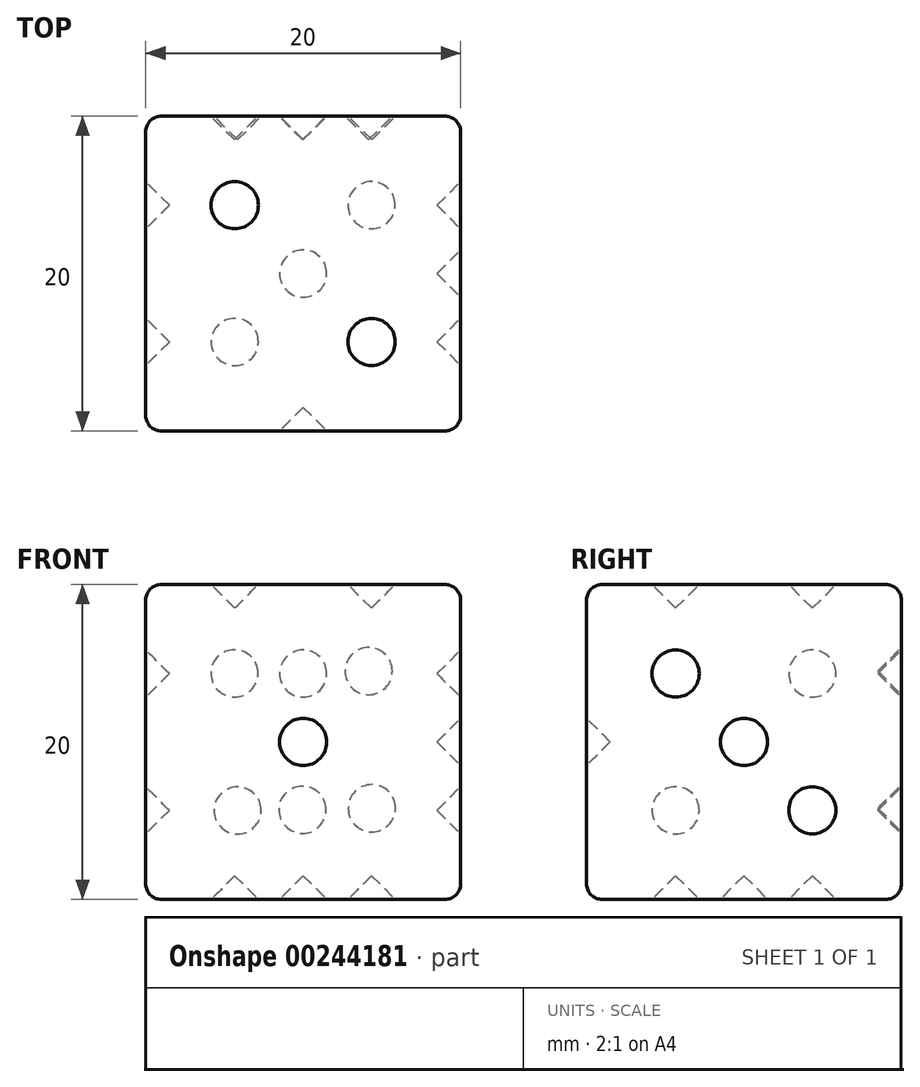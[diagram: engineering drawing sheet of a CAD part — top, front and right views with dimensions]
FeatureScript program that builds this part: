
annotation { "Feature Type Name" : "Feature", "Feature Type Description" : "" }
export const myFeature = defineFeature(function(context is Context, id is Id, definition is map)
    precondition{}
    {
        {
            var Q0;
            Q0=qCreatedBy(makeId("Top.planeOp"),FACE);
            var sketch = newSketch(context, id + "F0", { "sketchPlane" : qUnion([Q0])});
            skLineSegment(sketch, "E0.bottom", {"start": v(0, 0) * mm, "end": v(20, 0) * mm});
            skLineSegment(sketch, "E0.top", {"start": v(0, 20) * mm, "end": v(20, 20) * mm});
            skLineSegment(sketch, "E0.left", {"start": v(0, 0) * mm, "end": v(0, 20) * mm});
            skLineSegment(sketch, "E0.right", {"start": v(20, 0) * mm, "end": v(20, 20) * mm});
            skSolve(sketch);
        }
        {
            var Q0;
            Q0 = qSketchRegion(id + "F0", true);
            extrude(context, id + "F1", {"entities" : qUnion([Q0]), "depth" : 20 * mm});
        }
        {
            var Q0;
            Q0=makeQuery(id+"F1.opExtrude","SWEPT_FACE",FACE,{"disambiguationData":[OSD([sQuery(id+"F0.wireOp",EDGE,"E0.bottom")])]});
            var sketch = newSketch(context, id + "F2", { "sketchPlane" : qUnion([Q0])});
            skLineSegment(sketch, "E1", {"start": v(10, 20) * mm, "end": v(10, 0) * mm, "construction": true});
            skCircle(sketch, "E2", {"center": v(10, 10) * mm, "radius": 1.5 * mm});
            skSolve(sketch);
        }
        {
            var Q0;
            Q0 = qSketchRegion(id + "F2", true);
            extrude(context, id + "F3", {"entities" : qUnion([Q0]), "operationType" : NewBodyOperationType.REMOVE, "oppositeDirection" : true, "depth" : 1.5 * mm});
        }
        {
            var Q0;
            Q0=makeQuery(id+"F1.opExtrude","CAP_EDGE",EDGE,{"disambiguationData":[OSD([sQuery(id+"F0.wireOp",EDGE,"E0.bottom")])],"isStart":false});
            var Q1;
            Q1=makeQuery(id+"F1.opExtrude","CAP_EDGE",EDGE,{"disambiguationData":[OSD([sQuery(id+"F0.wireOp",EDGE,"E0.right")])],"isStart":false});
            var Q2;
            Q2=makeQuery(id+"F1.opExtrude","SWEPT_EDGE",EDGE,{"disambiguationData":[OSD([sQuery(id+"F0.wireOp",EDGE,"E0.bottom"),sQuery(id+"F0.wireOp",EDGE,"E0.right")])]});
            var Q3;
            Q3=makeQuery(id+"F1.opExtrude","SWEPT_EDGE",EDGE,{"disambiguationData":[OSD([sQuery(id+"F0.wireOp",EDGE,"E0.bottom"),sQuery(id+"F0.wireOp",EDGE,"E0.left")])]});
            var Q4;
            Q4=makeQuery(id+"F1.opExtrude","CAP_EDGE",EDGE,{"disambiguationData":[OSD([sQuery(id+"F0.wireOp",EDGE,"E0.bottom")])],"isStart":true});
            var Q5;
            Q5=makeQuery(id+"F1.opExtrude","CAP_EDGE",EDGE,{"disambiguationData":[OSD([sQuery(id+"F0.wireOp",EDGE,"E0.right")])],"isStart":true});
            var Q6;
            Q6=makeQuery(id+"F1.opExtrude","CAP_EDGE",EDGE,{"disambiguationData":[OSD([sQuery(id+"F0.wireOp",EDGE,"E0.left")])],"isStart":false});
            var Q7;
            Q7=makeQuery(id+"F1.opExtrude","CAP_EDGE",EDGE,{"disambiguationData":[OSD([sQuery(id+"F0.wireOp",EDGE,"E0.top")])],"isStart":false});
            var Q8;
            Q8=makeQuery(id+"F1.opExtrude","CAP_EDGE",EDGE,{"disambiguationData":[OSD([sQuery(id+"F0.wireOp",EDGE,"E0.left")])],"isStart":true});
            var Q9;
            Q9=makeQuery(id+"F1.opExtrude","SWEPT_EDGE",EDGE,{"disambiguationData":[OSD([sQuery(id+"F0.wireOp",EDGE,"E0.top"),sQuery(id+"F0.wireOp",EDGE,"E0.left")])]});
            var Q10;
            Q10=makeQuery(id+"F1.opExtrude","SWEPT_EDGE",EDGE,{"disambiguationData":[OSD([sQuery(id+"F0.wireOp",EDGE,"E0.top"),sQuery(id+"F0.wireOp",EDGE,"E0.right")])]});
            var Q11;
            Q11=makeQuery(id+"F1.opExtrude","CAP_EDGE",EDGE,{"disambiguationData":[OSD([sQuery(id+"F0.wireOp",EDGE,"E0.top")])],"isStart":true});
            fillet(context, id + "F4", {"entities" : qUnion([Q0, Q1, Q2, Q3, Q4, Q5, Q6, Q7, Q8, Q9, Q10, Q11]), "radius" : 1 * mm, "tangentPropagation" : true, "allowEdgeOverflow" : false});
        }
        {
            var Q0;
            Q0=makeQuery(id+"F1.opExtrude","CAP_FACE",FACE,{"disambiguationData":[OSD([sQuery(id+"F0.wireOp",EDGE,"E0.bottom"),sQuery(id+"F0.wireOp",EDGE,"E0.top"),sQuery(id+"F0.wireOp",EDGE,"E0.left"),sQuery(id+"F0.wireOp",EDGE,"E0.right")])],"isStart":false});
            var sketch = newSketch(context, id + "F5", { "sketchPlane" : qUnion([Q0])});
            skLineSegment(sketch, "E3", {"start": v(0, 20) * mm, "end": v(5.66, 14.34) * mm, "construction": true});
            skLineSegment(sketch, "E4", {"start": v(20, 0) * mm, "end": v(14.34, 5.66) * mm, "construction": true});
            skCircle(sketch, "E5", {"center": v(5.66, 14.34) * mm, "radius": 1.5 * mm});
            skCircle(sketch, "E6", {"center": v(14.34, 5.66) * mm, "radius": 1.5 * mm});
            skSolve(sketch);
        }
        {
            var Q0;
            Q0=makeQuery(id+"F5.imprint","IMPRINT",FACE,{"disambiguationData":[TD([[makeQuery(id+"F5.imprint","IMPRINT",EDGE,{"derivedFrom":sQuery(id+"F5.wireOp",EDGE,"E5")}),1.0]])]});
            var Q1;
            Q1=makeQuery(id+"F5.imprint","IMPRINT",FACE,{"disambiguationData":[TD([[makeQuery(id+"F5.imprint","IMPRINT",EDGE,{"derivedFrom":sQuery(id+"F5.wireOp",EDGE,"E6")}),1.0]])]});
            var Q2;
            Q2=sQuery(id+"F5.wireOp",EDGE,"E5");
            var Q3;
            Q3=sQuery(id+"F5.wireOp",EDGE,"E6");
            extrude(context, id + "F6", {"entities" : qUnion([Q0, Q1]), "operationType" : NewBodyOperationType.REMOVE, "surfaceEntities" : qUnion([Q2, Q3]), "oppositeDirection" : true, "depth" : 1.5 * mm});
        }
        {
            var Q0;
            Q0=makeQuery(id+"F1.opExtrude","SWEPT_FACE",FACE,{"disambiguationData":[OSD([sQuery(id+"F0.wireOp",EDGE,"E0.right")])]});
            var sketch = newSketch(context, id + "F7", { "sketchPlane" : qUnion([Q0])});
            skCircle(sketch, "E7", {"center": v(10, 10) * mm, "radius": 1.5 * mm});
            skCircle(sketch, "E8", {"center": v(5.66, 14.34) * mm, "radius": 1.5 * mm});
            skCircle(sketch, "E9", {"center": v(14.34, 5.66) * mm, "radius": 1.5 * mm});
            skSolve(sketch);
        }
        {
            var Q0;
            Q0=makeQuery(id+"F7.imprint","IMPRINT",FACE,{"disambiguationData":[TD([[makeQuery(id+"F7.imprint","IMPRINT",EDGE,{"derivedFrom":sQuery(id+"F7.wireOp",EDGE,"E8")}),1.0]])]});
            var Q1;
            Q1=makeQuery(id+"F7.imprint","IMPRINT",FACE,{"disambiguationData":[TD([[makeQuery(id+"F7.imprint","IMPRINT",EDGE,{"derivedFrom":sQuery(id+"F7.wireOp",EDGE,"E7")}),1.0]])]});
            var Q2;
            Q2=makeQuery(id+"F7.imprint","IMPRINT",FACE,{"disambiguationData":[TD([[makeQuery(id+"F7.imprint","IMPRINT",EDGE,{"derivedFrom":sQuery(id+"F7.wireOp",EDGE,"E9")}),1.0]])]});
            extrude(context, id + "F8", {"entities" : qUnion([Q0, Q1, Q2]), "operationType" : NewBodyOperationType.REMOVE, "oppositeDirection" : true, "depth" : 1.5 * mm});
        }
        {
            var Q0;
            Q0=makeQuery(id+"F1.opExtrude","SWEPT_FACE",FACE,{"disambiguationData":[OSD([sQuery(id+"F0.wireOp",EDGE,"E0.left")])]});
            var sketch = newSketch(context, id + "F9", { "sketchPlane" : qUnion([Q0])});
            skCircle(sketch, "E10", {"center": v(-14.34, 14.34) * mm, "radius": 1.5 * mm});
            skCircle(sketch, "E11", {"center": v(-5.66, 14.34) * mm, "radius": 1.5 * mm});
            skCircle(sketch, "E12", {"center": v(-14.34, 5.66) * mm, "radius": 1.5 * mm});
            skCircle(sketch, "E13", {"center": v(-5.66, 5.66) * mm, "radius": 1.5 * mm});
            skSolve(sketch);
        }
        {
            var Q0;
            Q0=makeQuery(id+"F9.imprint","IMPRINT",FACE,{"disambiguationData":[TD([[makeQuery(id+"F9.imprint","IMPRINT",EDGE,{"derivedFrom":sQuery(id+"F9.wireOp",EDGE,"E10")}),1.0]])]});
            var Q1;
            Q1=makeQuery(id+"F9.imprint","IMPRINT",FACE,{"disambiguationData":[TD([[makeQuery(id+"F9.imprint","IMPRINT",EDGE,{"derivedFrom":sQuery(id+"F9.wireOp",EDGE,"E11")}),1.0]])]});
            var Q2;
            Q2=makeQuery(id+"F9.imprint","IMPRINT",FACE,{"disambiguationData":[TD([[makeQuery(id+"F9.imprint","IMPRINT",EDGE,{"derivedFrom":sQuery(id+"F9.wireOp",EDGE,"E12")}),1.0]])]});
            var Q3;
            Q3=makeQuery(id+"F9.imprint","IMPRINT",FACE,{"disambiguationData":[TD([[makeQuery(id+"F9.imprint","IMPRINT",EDGE,{"derivedFrom":sQuery(id+"F9.wireOp",EDGE,"E13")}),1.0]])]});
            extrude(context, id + "F10", {"entities" : qUnion([Q0, Q1, Q2, Q3]), "operationType" : NewBodyOperationType.REMOVE, "oppositeDirection" : true, "depth" : 1.5 * mm});
        }
        {
            var Q0;
            Q0=makeQuery(id+"F1.opExtrude","CAP_FACE",FACE,{"disambiguationData":[OSD([sQuery(id+"F0.wireOp",EDGE,"E0.bottom"),sQuery(id+"F0.wireOp",EDGE,"E0.top"),sQuery(id+"F0.wireOp",EDGE,"E0.left"),sQuery(id+"F0.wireOp",EDGE,"E0.right")])],"isStart":true});
            var sketch = newSketch(context, id + "F11", { "sketchPlane" : qUnion([Q0])});
            skCircle(sketch, "E14", {"center": v(5.66, -5.66) * mm, "radius": 1.5 * mm});
            skCircle(sketch, "E15", {"center": v(14.34, -5.66) * mm, "radius": 1.5 * mm});
            skCircle(sketch, "E16", {"center": v(5.66, -14.34) * mm, "radius": 1.5 * mm});
            skCircle(sketch, "E17", {"center": v(14.34, -14.34) * mm, "radius": 1.5 * mm});
            skCircle(sketch, "E18", {"center": v(10, -10) * mm, "radius": 1.5 * mm});
            skSolve(sketch);
        }
        {
            var Q0;
            Q0=makeQuery(id+"F11.imprint","IMPRINT",FACE,{"disambiguationData":[TD([[makeQuery(id+"F11.imprint","IMPRINT",EDGE,{"derivedFrom":sQuery(id+"F11.wireOp",EDGE,"E14")}),1.0]])]});
            var Q1;
            Q1=makeQuery(id+"F11.imprint","IMPRINT",FACE,{"disambiguationData":[TD([[makeQuery(id+"F11.imprint","IMPRINT",EDGE,{"derivedFrom":sQuery(id+"F11.wireOp",EDGE,"E18")}),1.0]])]});
            var Q2;
            Q2=makeQuery(id+"F11.imprint","IMPRINT",FACE,{"disambiguationData":[TD([[makeQuery(id+"F11.imprint","IMPRINT",EDGE,{"derivedFrom":sQuery(id+"F11.wireOp",EDGE,"E15")}),1.0]])]});
            var Q3;
            Q3=makeQuery(id+"F11.imprint","IMPRINT",FACE,{"disambiguationData":[TD([[makeQuery(id+"F11.imprint","IMPRINT",EDGE,{"derivedFrom":sQuery(id+"F11.wireOp",EDGE,"E16")}),1.0]])]});
            var Q4;
            Q4=makeQuery(id+"F11.imprint","IMPRINT",FACE,{"disambiguationData":[TD([[makeQuery(id+"F11.imprint","IMPRINT",EDGE,{"derivedFrom":sQuery(id+"F11.wireOp",EDGE,"E17")}),1.0]])]});
            extrude(context, id + "F12", {"entities" : qUnion([Q0, Q1, Q2, Q3, Q4]), "operationType" : NewBodyOperationType.REMOVE, "oppositeDirection" : true, "depth" : 1.5 * mm});
        }
        {
            var Q0;
            Q0=makeQuery(id+"F1.opExtrude","SWEPT_FACE",FACE,{"disambiguationData":[OSD([sQuery(id+"F0.wireOp",EDGE,"E0.top")])]});
            var sketch = newSketch(context, id + "F13", { "sketchPlane" : qUnion([Q0])});
            skCircle(sketch, "E19", {"center": v(-5.64, 14.36) * mm, "radius": 1.5 * mm});
            skCircle(sketch, "E20", {"center": v(-5.83, 5.65) * mm, "radius": 1.5 * mm});
            skCircle(sketch, "E21", {"center": v(-14.16, 14.5) * mm, "radius": 1.5 * mm});
            skCircle(sketch, "E22", {"center": v(-14.36, 5.79) * mm, "radius": 1.5 * mm});
            skCircle(sketch, "E23", {"center": v(-10, 14.34) * mm, "radius": 1.5 * mm});
            skCircle(sketch, "E24", {"center": v(-9.96, 5.69) * mm, "radius": 1.5 * mm});
            skSolve(sketch);
        }
        {
            var Q0;
            Q0=makeQuery(id+"F13.imprint","IMPRINT",FACE,{"disambiguationData":[TD([[makeQuery(id+"F13.imprint","IMPRINT",EDGE,{"derivedFrom":sQuery(id+"F13.wireOp",EDGE,"E19")}),1.0]])]});
            var Q1;
            Q1=makeQuery(id+"F13.imprint","IMPRINT",FACE,{"disambiguationData":[TD([[makeQuery(id+"F13.imprint","IMPRINT",EDGE,{"derivedFrom":sQuery(id+"F13.wireOp",EDGE,"E23")}),1.0]])]});
            var Q2;
            Q2=makeQuery(id+"F13.imprint","IMPRINT",FACE,{"disambiguationData":[TD([[makeQuery(id+"F13.imprint","IMPRINT",EDGE,{"derivedFrom":sQuery(id+"F13.wireOp",EDGE,"E21")}),1.0]])]});
            var Q3;
            Q3=makeQuery(id+"F13.imprint","IMPRINT",FACE,{"disambiguationData":[TD([[makeQuery(id+"F13.imprint","IMPRINT",EDGE,{"derivedFrom":sQuery(id+"F13.wireOp",EDGE,"E22")}),1.0]])]});
            var Q4;
            Q4=makeQuery(id+"F13.imprint","IMPRINT",FACE,{"disambiguationData":[TD([[makeQuery(id+"F13.imprint","IMPRINT",EDGE,{"derivedFrom":sQuery(id+"F13.wireOp",EDGE,"E24")}),1.0]])]});
            var Q5;
            Q5=makeQuery(id+"F13.imprint","IMPRINT",FACE,{"disambiguationData":[TD([[makeQuery(id+"F13.imprint","IMPRINT",EDGE,{"derivedFrom":sQuery(id+"F13.wireOp",EDGE,"E20")}),1.0]])]});
            extrude(context, id + "F14", {"entities" : qUnion([Q0, Q1, Q2, Q3, Q4, Q5]), "operationType" : NewBodyOperationType.REMOVE, "oppositeDirection" : true, "depth" : 1.5 * mm});
        }
        {
            var Q0;
            Q0=makeQuery(id+"F3.boolean.opBoolean","COPY",EDGE,{"derivedFrom":makeQuery(id+"F3.opExtrude","CAP_EDGE",EDGE,{"disambiguationData":[OSD([sQuery(id+"F2.wireOp",EDGE,"E2")])],"isStart":false})});
            var Q1;
            Q1=makeQuery(id+"F6.boolean.opBoolean","COPY",FACE,{"derivedFrom":makeQuery(id+"F6.opExtrude","CAP_FACE",FACE,{"disambiguationData":[OSD([sQuery(id+"F5.wireOp",EDGE,"E5")])],"isStart":false})});
            var Q2;
            Q2=makeQuery(id+"F6.boolean.opBoolean","COPY",FACE,{"derivedFrom":makeQuery(id+"F6.opExtrude","CAP_FACE",FACE,{"disambiguationData":[OSD([sQuery(id+"F5.wireOp",EDGE,"E6")])],"isStart":false})});
            var Q3;
            Q3=makeQuery(id+"F8.boolean.opBoolean","COPY",FACE,{"derivedFrom":makeQuery(id+"F8.opExtrude","CAP_FACE",FACE,{"disambiguationData":[OSD([sQuery(id+"F7.wireOp",EDGE,"E8")])],"isStart":false})});
            var Q4;
            Q4=makeQuery(id+"F8.boolean.opBoolean","COPY",FACE,{"derivedFrom":makeQuery(id+"F8.opExtrude","CAP_FACE",FACE,{"disambiguationData":[OSD([sQuery(id+"F7.wireOp",EDGE,"E7")])],"isStart":false})});
            var Q5;
            Q5=makeQuery(id+"F8.boolean.opBoolean","COPY",FACE,{"derivedFrom":makeQuery(id+"F8.opExtrude","CAP_FACE",FACE,{"disambiguationData":[OSD([sQuery(id+"F7.wireOp",EDGE,"E9")])],"isStart":false})});
            var Q6;
            Q6=makeQuery(id+"F10.boolean.opBoolean","COPY",FACE,{"derivedFrom":makeQuery(id+"F10.opExtrude","CAP_FACE",FACE,{"disambiguationData":[OSD([sQuery(id+"F9.wireOp",EDGE,"E12")])],"isStart":false})});
            var Q7;
            Q7=makeQuery(id+"F10.boolean.opBoolean","COPY",FACE,{"derivedFrom":makeQuery(id+"F10.opExtrude","CAP_FACE",FACE,{"disambiguationData":[OSD([sQuery(id+"F9.wireOp",EDGE,"E10")])],"isStart":false})});
            var Q8;
            Q8=makeQuery(id+"F10.boolean.opBoolean","COPY",FACE,{"derivedFrom":makeQuery(id+"F10.opExtrude","CAP_FACE",FACE,{"disambiguationData":[OSD([sQuery(id+"F9.wireOp",EDGE,"E11")])],"isStart":false})});
            var Q9;
            Q9=makeQuery(id+"F10.boolean.opBoolean","COPY",FACE,{"derivedFrom":makeQuery(id+"F10.opExtrude","CAP_FACE",FACE,{"disambiguationData":[OSD([sQuery(id+"F9.wireOp",EDGE,"E13")])],"isStart":false})});
            var Q10;
            Q10=makeQuery(id+"F12.boolean.opBoolean","COPY",FACE,{"derivedFrom":makeQuery(id+"F12.opExtrude","CAP_FACE",FACE,{"disambiguationData":[OSD([sQuery(id+"F11.wireOp",EDGE,"E14")])],"isStart":false})});
            var Q11;
            Q11=makeQuery(id+"F12.boolean.opBoolean","COPY",FACE,{"derivedFrom":makeQuery(id+"F12.opExtrude","CAP_FACE",FACE,{"disambiguationData":[OSD([sQuery(id+"F11.wireOp",EDGE,"E15")])],"isStart":false})});
            var Q12;
            Q12=makeQuery(id+"F12.boolean.opBoolean","COPY",FACE,{"derivedFrom":makeQuery(id+"F12.opExtrude","CAP_FACE",FACE,{"disambiguationData":[OSD([sQuery(id+"F11.wireOp",EDGE,"E18")])],"isStart":false})});
            var Q13;
            Q13=makeQuery(id+"F12.boolean.opBoolean","COPY",FACE,{"derivedFrom":makeQuery(id+"F12.opExtrude","CAP_FACE",FACE,{"disambiguationData":[OSD([sQuery(id+"F11.wireOp",EDGE,"E16")])],"isStart":false})});
            var Q14;
            Q14=makeQuery(id+"F12.boolean.opBoolean","COPY",FACE,{"derivedFrom":makeQuery(id+"F12.opExtrude","CAP_FACE",FACE,{"disambiguationData":[OSD([sQuery(id+"F11.wireOp",EDGE,"E17")])],"isStart":false})});
            var Q15;
            Q15=makeQuery(id+"F14.boolean.opBoolean","COPY",FACE,{"derivedFrom":makeQuery(id+"F14.opExtrude","CAP_FACE",FACE,{"disambiguationData":[OSD([sQuery(id+"F13.wireOp",EDGE,"E19")])],"isStart":false})});
            var Q16;
            Q16=makeQuery(id+"F14.boolean.opBoolean","COPY",FACE,{"derivedFrom":makeQuery(id+"F14.opExtrude","CAP_FACE",FACE,{"disambiguationData":[OSD([sQuery(id+"F13.wireOp",EDGE,"E23")])],"isStart":false})});
            var Q17;
            Q17=makeQuery(id+"F14.boolean.opBoolean","COPY",FACE,{"derivedFrom":makeQuery(id+"F14.opExtrude","CAP_FACE",FACE,{"disambiguationData":[OSD([sQuery(id+"F13.wireOp",EDGE,"E21")])],"isStart":false})});
            var Q18;
            Q18=makeQuery(id+"F14.boolean.opBoolean","COPY",FACE,{"derivedFrom":makeQuery(id+"F14.opExtrude","CAP_FACE",FACE,{"disambiguationData":[OSD([sQuery(id+"F13.wireOp",EDGE,"E22")])],"isStart":false})});
            var Q19;
            Q19=makeQuery(id+"F14.boolean.opBoolean","COPY",FACE,{"derivedFrom":makeQuery(id+"F14.opExtrude","CAP_FACE",FACE,{"disambiguationData":[OSD([sQuery(id+"F13.wireOp",EDGE,"E24")])],"isStart":false})});
            var Q20;
            Q20=makeQuery(id+"F14.boolean.opBoolean","COPY",FACE,{"derivedFrom":makeQuery(id+"F14.opExtrude","CAP_FACE",FACE,{"disambiguationData":[OSD([sQuery(id+"F13.wireOp",EDGE,"E20")])],"isStart":false})});
            chamfer(context, id + "F15", {"entities" : qUnion([Q0, Q1, Q2, Q3, Q4, Q5, Q6, Q7, Q8, Q9, Q10, Q11, Q12, Q13, Q14, Q15, Q16, Q17, Q18, Q19, Q20]), "width" : 1.5 * mm, "tangentPropagation" : true});
        }
    });
